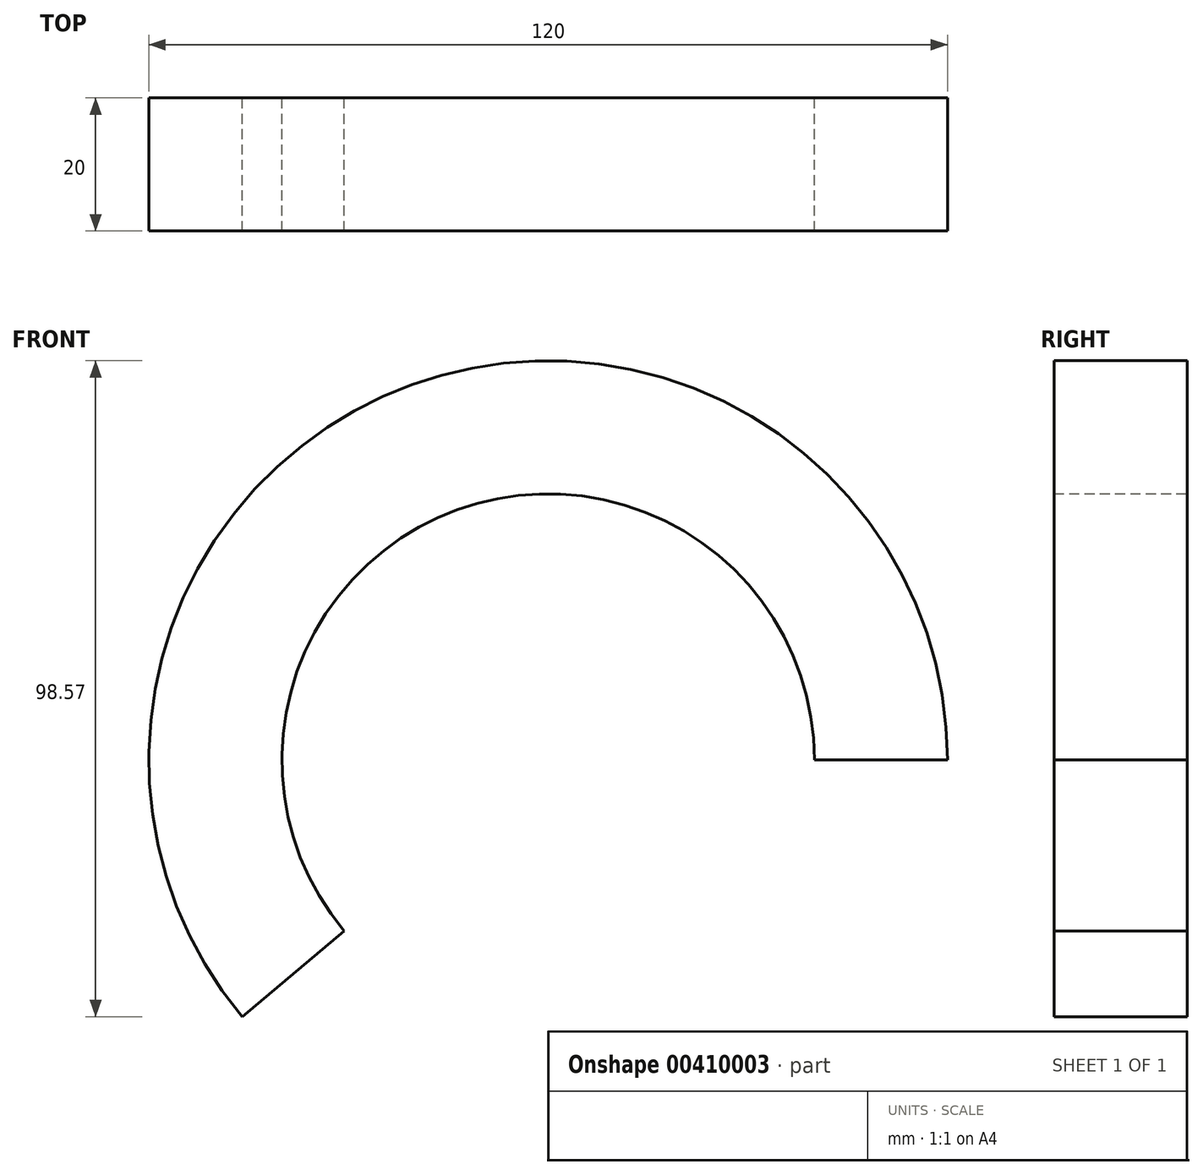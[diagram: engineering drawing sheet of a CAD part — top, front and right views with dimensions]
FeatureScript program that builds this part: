
annotation { "Feature Type Name" : "Feature", "Feature Type Description" : "" }
export const myFeature = defineFeature(function(context is Context, id is Id, definition is map)
    precondition{}
    {
        {
            var Q0;
            Q0=qCreatedBy(makeId("Top.planeOp"),FACE);
            var sketch = newSketch(context, id + "F0", { "sketchPlane" : qUnion([Q0])});
            skLineSegment(sketch, "E0", {"start": v(0, 36.57) * mm, "end": v(0, -36.57) * mm, "construction": true});
            skLineSegment(sketch, "E1", {"start": v(-65.9, 0) * mm, "end": v(65.9, 0) * mm, "construction": true});
            skLineSegment(sketch, "E2.bottom", {"start": v(10, -10) * mm, "end": v(-10, -10) * mm});
            skLineSegment(sketch, "E2.top", {"start": v(10, 10) * mm, "end": v(-10, 10) * mm});
            skLineSegment(sketch, "E2.left", {"start": v(10, -10) * mm, "end": v(10, 10) * mm});
            skLineSegment(sketch, "E2.right", {"start": v(-10, -10) * mm, "end": v(-10, 10) * mm});
            skPoint(sketch, "E2.middle", {"position": v(0, 0) * mm});
            skLineSegment(sketch, "E3", {"start": v(-50, 32.8) * mm, "end": v(-50, -33.25) * mm, "construction": true});
            skSolve(sketch);
        }
        {
            var Q0;
            Q0 = qSketchRegion(id + "F0", true);
            var Q1;
            Q1=sQuery(id+"F0.wireOp",EDGE,"E3");
            revolve(context, id + "F1", {"entities" : qUnion([Q0]), "axis" : qUnion([Q1]), "revolveType" : RevolveType.ONE_DIRECTION, "angle" : 220 * degree});
        }
    });
